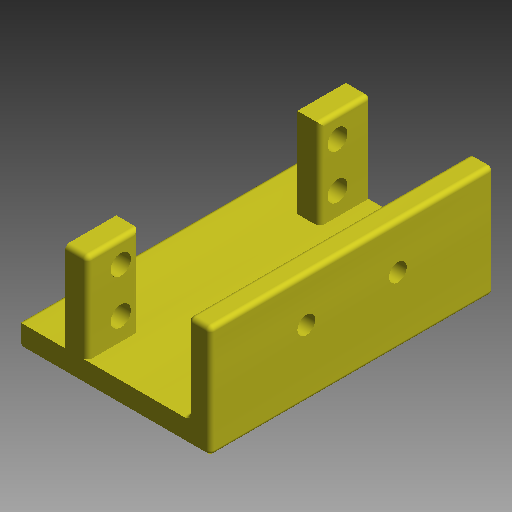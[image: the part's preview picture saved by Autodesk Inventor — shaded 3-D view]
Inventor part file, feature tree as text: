
AUTODESK INVENTOR PART (.ipt)
format: ipt  version: 2017 (Build 210142000, 142)  size: 202,240 bytes
history: native  units: mm (DEFAULTED — no unit token found)
features: extrude x4, sketch x4, fillet x1
ambient origin geometry x8: Origin, YZ Plane, XZ Plane, XY Plane, X Axis, Y Axis, Z Axis, Center Point
bodies: Body1 (feature_tree)
feature tree (9):
  extrude  "Extrusion8"  Depth=63.5mm
  extrude  "Extrusion9"  TaperAngle=0.0deg  [1 undecoded]
  extrude  "Extrusion10"  Depth=5.0mm
  fillet  "Fillet1"  Radius=15.5mm
  extrude  "Extrusion11"  TaperAngle=0.0deg  [1 undecoded]
  sketch  "Sketch8"  dims[d31=43.0mm d32=63.5mm]
  sketch  "Sketch9"  dims[d33=5.0mm d34=0.0mm]
  sketch  "Sketch10"  dims[d35=11.5mm d36=5.0mm d38=15.5mm]
  sketch  "Sketch11"  dims[d39=20.0mm d40=0.0mm d41=5.0mm d42=4.0mm d43=10.0mm d44=21.5mm d45=10.0mm d46=0.0mm d47=21.5mm d48=1.0mm d51=2.75mm d52=4.5mm d53=7.5mm d54=2.75mm d56=7.5mm d57=10.0mm d58=0.0mm]
note: 2 required parameter values undecoded (feature->parameter linkage not recoverable at this tier; creation-order binding heuristic only, values carry confidence <= 0.55)
